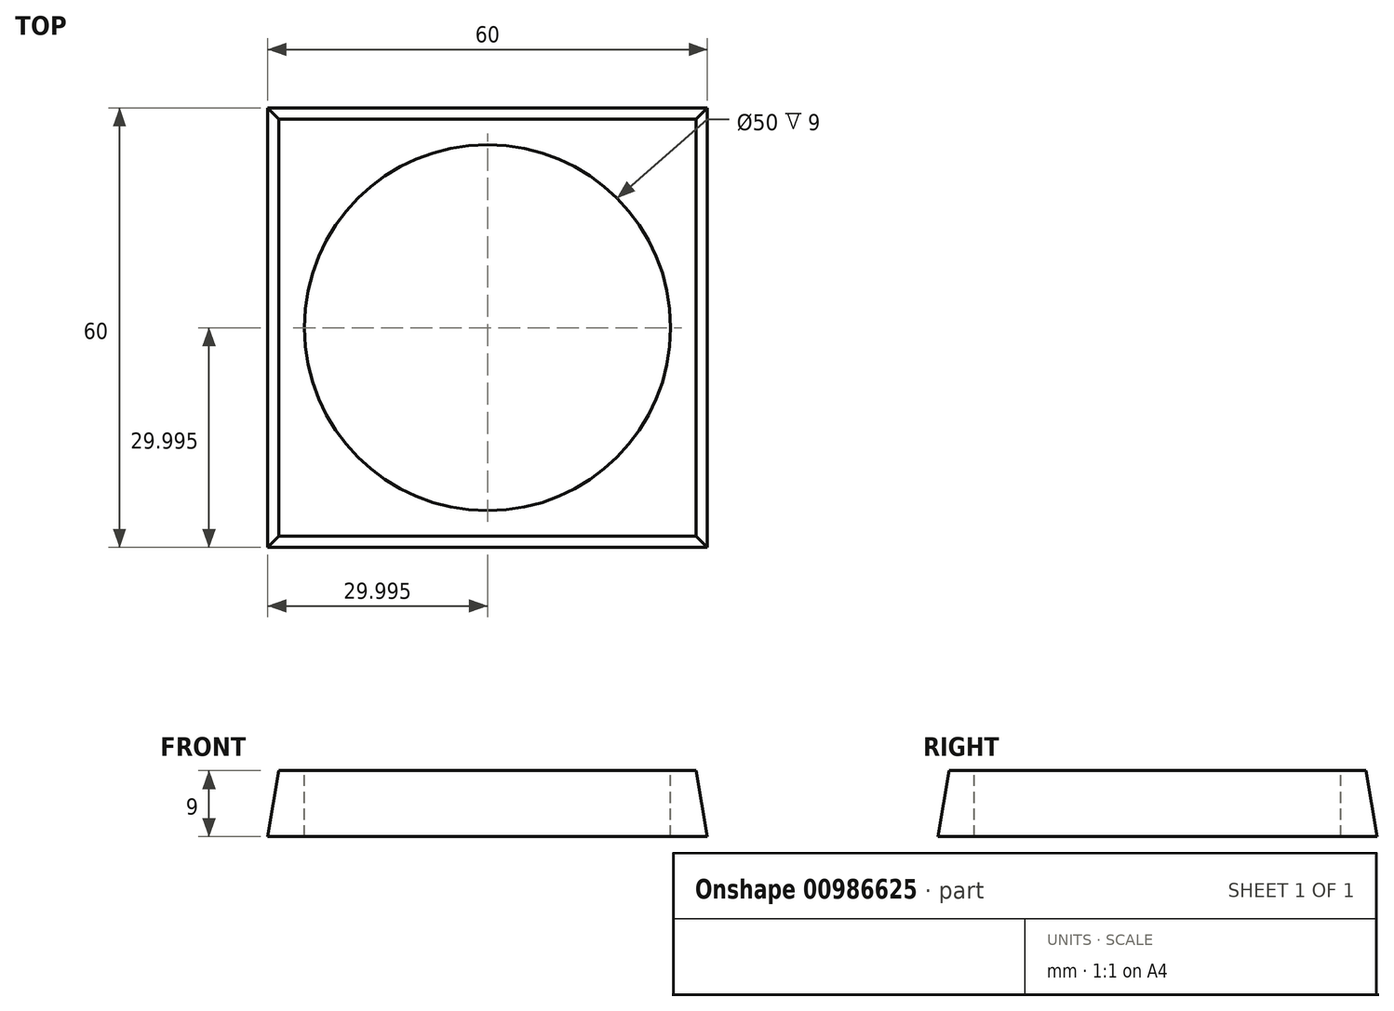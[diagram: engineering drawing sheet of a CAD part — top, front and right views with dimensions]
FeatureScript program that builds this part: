
annotation { "Feature Type Name" : "Feature", "Feature Type Description" : "" }
export const myFeature = defineFeature(function(context is Context, id is Id, definition is map)
    precondition{}
    {
        {
            var Q0;
            Q0=qCreatedBy(makeId("Top.planeOp"),FACE);
            var sketch = newSketch(context, id + "F0", { "sketchPlane" : qUnion([Q0])});
            skLineSegment(sketch, "E0.bottom", {"start": v(-13.04, 52.43) * mm, "end": v(46.96, 52.43) * mm});
            skLineSegment(sketch, "E0.top", {"start": v(-13.04, -7.57) * mm, "end": v(46.96, -7.57) * mm});
            skLineSegment(sketch, "E0.left", {"start": v(-13.04, 52.43) * mm, "end": v(-13.04, -7.57) * mm});
            skLineSegment(sketch, "E0.right", {"start": v(46.96, 52.43) * mm, "end": v(46.96, -7.57) * mm});
            skSolve(sketch);
        }
        {
            var Q0;
            Q0=qSketchRegion(id+"F0",true);
            extrude(context, id + "F1", {"entities" : qUnion([Q0]), "depth" : 9 * mm, "offsetDistance" : 25 * mm});
        }
        {
            var Q0;
            Q0=qCreatedBy(makeId("Right.planeOp"),FACE);
            var sketch = newSketch(context, id + "F2", { "sketchPlane" : qUnion([Q0])});
            skLineSegment(sketch, "E1", {"start": v(-7.57, 0) * mm, "end": v(-7.57, 9) * mm});
            skLineSegment(sketch, "E2", {"start": v(-7.57, 0) * mm, "end": v(-6.04, 9) * mm});
            skLineSegment(sketch, "E3", {"start": v(-6.04, 9) * mm, "end": v(-7.57, 9) * mm});
            skLineSegment(sketch, "E4", {"start": v(52.43, 0) * mm, "end": v(52.43, 9) * mm});
            skLineSegment(sketch, "E5", {"start": v(52.43, 9) * mm, "end": v(50.89, 9) * mm});
            skLineSegment(sketch, "E6", {"start": v(50.89, 9) * mm, "end": v(52.43, 0) * mm});
            skSolve(sketch);
        }
        {
            var Q0;
            Q0=qCreatedBy(makeId("Front.planeOp"),FACE);
            var sketch = newSketch(context, id + "F3", { "sketchPlane" : qUnion([Q0])});
            skLineSegment(sketch, "E7", {"start": v(-13.04, 0) * mm, "end": v(-13.04, 9) * mm});
            skLineSegment(sketch, "E8", {"start": v(-13.04, 9) * mm, "end": v(-11.5, 9) * mm});
            skLineSegment(sketch, "E9", {"start": v(-11.5, 9) * mm, "end": v(-13.04, 0) * mm});
            skLineSegment(sketch, "E10", {"start": v(46.96, 0) * mm, "end": v(46.96, 9) * mm});
            skLineSegment(sketch, "E11", {"start": v(46.96, 9) * mm, "end": v(45.42, 9) * mm});
            skLineSegment(sketch, "E12", {"start": v(45.42, 9) * mm, "end": v(46.96, 0) * mm});
            skSolve(sketch);
        }
        {
            var Q0;
            Q0=qSketchRegion(id+"F2",true);
            extrude(context, id + "F4", {"entities" : qUnion([Q0]), "operationType" : NewBodyOperationType.REMOVE, "oppositeDirection" : true, "depth" : 25 * mm, "offsetDistance" : 25 * mm});
        }
        {
            var Q0;
            Q0=qSketchRegion(id+"F2",true);
            extrude(context, id + "F5", {"entities" : qUnion([Q0]), "operationType" : NewBodyOperationType.REMOVE, "depth" : 50 * mm, "offsetDistance" : 25 * mm});
        }
        {
            var Q0;
            Q0=qSketchRegion(id+"F3",true);
            extrude(context, id + "F6", {"entities" : qUnion([Q0]), "operationType" : NewBodyOperationType.REMOVE, "oppositeDirection" : true, "depth" : 55 * mm, "offsetDistance" : 25 * mm});
        }
        {
            var Q0;
            Q0=qSketchRegion(id+"F3",true);
            extrude(context, id + "F7", {"entities" : qUnion([Q0]), "operationType" : NewBodyOperationType.REMOVE, "depth" : 25 * mm, "offsetDistance" : 25 * mm});
        }
        {
            var Q0;
            Q0=makeQuery(id+"F1.opExtrude","CAP_FACE",FACE,{"disambiguationData":[OSD([sQuery(id+"F0.wireOp",EDGE,"E0.bottom"),sQuery(id+"F0.wireOp",EDGE,"E0.top"),sQuery(id+"F0.wireOp",EDGE,"E0.left"),sQuery(id+"F0.wireOp",EDGE,"E0.right")])],"isStart":false});
            var sketch = newSketch(context, id + "F8", { "sketchPlane" : qUnion([Q0])});
            skLineSegment(sketch, "E13", {"start": v(-11.5, 50.89) * mm, "end": v(-11.5, -6.04) * mm});
            skLineSegment(sketch, "E14", {"start": v(-11.5, -6.04) * mm, "end": v(45.42, -6.04) * mm});
            skLineSegment(sketch, "E15", {"start": v(-11.5, 50.89) * mm, "end": v(45.42, -6.04) * mm});
            skLineSegment(sketch, "E16", {"start": v(45.42, 50.89) * mm, "end": v(16.96, 22.43) * mm});
            skSolve(sketch);
        }
        {
            var Q0;
            Q0=sQuery(id+"F8.wireOp",VERTEX,"E16.end");
            var Q1;
            Q1=makeQuery(id+"F1.opExtrude","SWEPT_BODY",BODY,{"disambiguationData":[OSD([sQuery(id+"F0.wireOp",EDGE,"E0.bottom"),sQuery(id+"F0.wireOp",EDGE,"E0.top"),sQuery(id+"F0.wireOp",EDGE,"E0.left"),sQuery(id+"F0.wireOp",EDGE,"E0.right")])]});
            hole(context, id + "F9", {"style" : HoleStyle.SIMPLE, "endStyle" : HoleEndStyle.THROUGH, "holeDiameter" : 50 * mm, "majorDiameter" : 5 * mm, "isTappedThrough" : true, "tappedDepth" : 12 * mm, "tapClearance" : 3, "locations" : qUnion([Q0]), "scope" : qUnion([Q1])});
        }
    });
